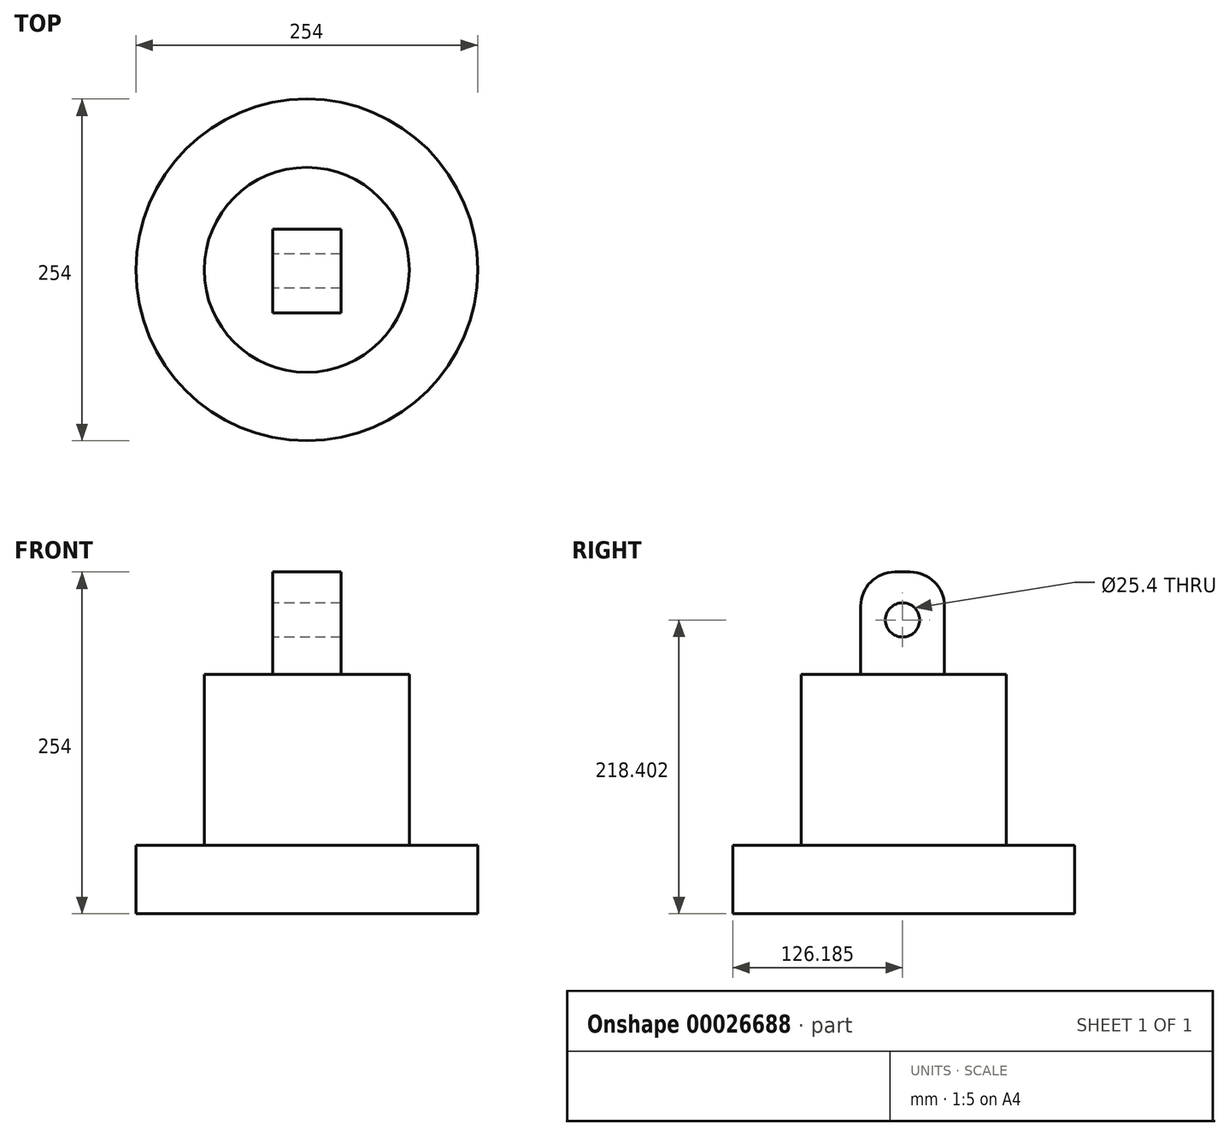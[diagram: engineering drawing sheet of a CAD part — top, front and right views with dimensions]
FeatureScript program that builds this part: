
annotation { "Feature Type Name" : "Feature", "Feature Type Description" : "" }
export const myFeature = defineFeature(function(context is Context, id is Id, definition is map)
    precondition{}
    {
        {
            var Q0;
            Q0=qCreatedBy(makeId("Front.planeOp"),FACE);
            var sketch = newSketch(context, id + "F0", { "sketchPlane" : qUnion([Q0])});
            skLineSegment(sketch, "E0", {"start": v(-155.87, 46) * mm, "end": v(-155.87, -4.8) * mm});
            skLineSegment(sketch, "E1", {"start": v(-155.87, -4.8) * mm, "end": v(-28.87, -4.8) * mm});
            skLineSegment(sketch, "E2", {"start": v(-28.87, -4.8) * mm, "end": v(-28.87, 46) * mm});
            skLineSegment(sketch, "E3", {"start": v(-28.87, 46) * mm, "end": v(-155.87, 46) * mm});
            skSolve(sketch);
        }
        {
            var Q0;
            Q0=makeQuery(id+"F0.imprint","IMPRINT",FACE,{"disambiguationData":[TD([[makeQuery(id+"F0.imprint","IMPRINT",EDGE,{"derivedFrom":sQuery(id+"F0.wireOp",EDGE,"E0")}),1.0]])]});
            var Q1;
            Q1=sQuery(id+"F0.wireOp",EDGE,"E0");
            revolve(context, id + "F1", {"entities" : qUnion([Q0]), "axis" : qUnion([Q1]), "revolveType" : RevolveType.FULL});
        }
        {
            var Q0;
            Q0=makeQuery(id+"F1.opRevolve","SWEPT_FACE",FACE,{"disambiguationData":[OSD([sQuery(id+"F0.wireOp",EDGE,"E3")])]});
            var sketch = newSketch(context, id + "F2", { "sketchPlane" : qUnion([Q0])});
            skCircle(sketch, "E4", {"center": v(-155.87, 0) * mm, "radius": 76.2 * mm});
            skSolve(sketch);
        }
        {
            var Q0;
            Q0 = qSketchRegion(id + "F2", true);
            extrude(context, id + "F3", {"entities" : qUnion([Q0]), "operationType" : NewBodyOperationType.ADD, "depth" : 127 * mm});
        }
        {
            var Q0;
            Q0=makeQuery(id+"F3.opExtrude","CAP_FACE",FACE,{"disambiguationData":[OSD([sQuery(id+"F2.wireOp",EDGE,"E4")])],"isStart":false});
            var sketch = newSketch(context, id + "F4", { "sketchPlane" : qUnion([Q0])});
            skLineSegment(sketch, "E5", {"start": v(-155.87, 30.3) * mm, "end": v(-130.47, 30.3) * mm});
            skLineSegment(sketch, "E6", {"start": v(-130.47, 30.3) * mm, "end": v(-130.47, -31.94) * mm});
            skLineSegment(sketch, "E7", {"start": v(-130.47, -31.94) * mm, "end": v(-155.87, -31.94) * mm});
            skLineSegment(sketch, "E8", {"start": v(-155.87, 30.3) * mm, "end": v(-181.27, 30.3) * mm});
            skLineSegment(sketch, "E9", {"start": v(-181.27, 30.3) * mm, "end": v(-181.27, -31.94) * mm});
            skLineSegment(sketch, "E10", {"start": v(-181.27, -31.94) * mm, "end": v(-155.87, -31.94) * mm});
            skPoint(sketch, "E11.start.orphan", {"position": v(-155.87, 0) * mm});
            skSolve(sketch);
        }
        {
            var Q0;
            Q0=makeQuery(id+"F4.imprint","IMPRINT",FACE,{"disambiguationData":[TD([[makeQuery(id+"F4.imprint","IMPRINT",EDGE,{"derivedFrom":sQuery(id+"F4.wireOp",EDGE,"E5")}),-1.0]])]});
            extrude(context, id + "F5", {"entities" : qUnion([Q0]), "operationType" : NewBodyOperationType.ADD, "depth" : 76.2 * mm});
        }
        {
            var Q0;
            Q0=makeQuery(id+"F5.opExtrude","CAP_EDGE",EDGE,{"disambiguationData":[OSD([sQuery(id+"F4.wireOp",EDGE,"E5"),sQuery(id+"F4.wireOp",EDGE,"E8")])],"isStart":false});
            fillet(context, id + "F6", {"entities" : qUnion([Q0]), "radius" : 25.4 * mm, "tangentPropagation" : true, "allowEdgeOverflow" : false});
        }
        {
            var Q0;
            Q0=makeQuery(id+"F5.opExtrude","CAP_EDGE",EDGE,{"disambiguationData":[OSD([sQuery(id+"F4.wireOp",EDGE,"E7"),sQuery(id+"F4.wireOp",EDGE,"E10")])],"isStart":false});
            fillet(context, id + "F7", {"entities" : qUnion([Q0]), "radius" : 25.4 * mm, "tangentPropagation" : true, "allowEdgeOverflow" : false});
        }
        {
            var Q0;
            Q0=makeQuery(id+"F5.opExtrude","SWEPT_FACE",FACE,{"disambiguationData":[OSD([sQuery(id+"F4.wireOp",EDGE,"E9")])]});
            var sketch = newSketch(context, id + "F8", { "sketchPlane" : qUnion([Q0])});
            skCircle(sketch, "E12", {"center": v(0.81, 213.61) * mm, "radius": 12.7 * mm});
            skSolve(sketch);
        }
        {
            var Q0;
            Q0=makeQuery(id+"F8.imprint","IMPRINT",FACE,{"disambiguationData":[TD([[makeQuery(id+"F8.imprint","IMPRINT",EDGE,{"derivedFrom":sQuery(id+"F8.wireOp",EDGE,"E12")}),1.0]])]});
            extrude(context, id + "F9", {"entities" : qUnion([Q0]), "operationType" : NewBodyOperationType.REMOVE, "endBound" : BoundingType.THROUGH_ALL, "oppositeDirection" : true, "depth" : 25.4 * mm});
        }
    });
